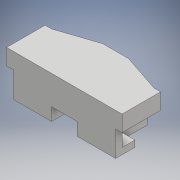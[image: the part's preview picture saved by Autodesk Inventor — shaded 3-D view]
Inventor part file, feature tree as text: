
AUTODESK INVENTOR PART (.ipt)
format: ipt  version: 2017 (Build 210142000, 142)  size: 303,104 bytes
history: native  units: mm
features: extrude x22, sketch x22, projected_geometry x2
ambient origin geometry x8: Origin, YZ Plane, XZ Plane, XY Plane, X Axis, Y Axis, Z Axis, Center Point
bodies: Solid1 (feature_tree)
feature tree (46):
  extrude  "Extrusion1"  Depth=60.0mm
  extrude  "Extrusion2"  Depth=10.0mm
  extrude  "Extrusion3"  Depth=160.0mm
  extrude  "Extrusion4"  Depth=70.0mm TaperAngle=0.0deg
  extrude  "Extrusion5"  Depth=10.0mm
  extrude  "Extrusion6"  Depth=10.0mm TaperAngle=0.0deg
  extrude  "Extrusion7"  Depth=50.0mm
  extrude  "Extrusion8"  Depth=50.0mm
  extrude  "Extrusion9"  Depth=10.0mm
  extrude  "Extrusion10"  Depth=10.0mm TaperAngle=0.0deg
  extrude  "Extrusion11"  Depth=60.0mm
  extrude  "Extrusion12"  Depth=60.0mm
  extrude  "Extrusion13"  Depth=10.0mm TaperAngle=0.0deg
  extrude  "Extrusion14"  Depth=10.0mm TaperAngle=0.0deg
  extrude  "Extrusion15"  Depth=160.0mm
  extrude  "Extrusion16"  Depth=20.0mm TaperAngle=0.0deg
  extrude  "Extrusion17"  Depth=15.0mm
  extrude  "Extrusion18"  Depth=15.0mm
  extrude  "Extrusion19"  Depth=10.0mm TaperAngle=0.0deg
  extrude  "Extrusion20"  Depth=10.0mm TaperAngle=0.0deg
  extrude  "Extrusion21"  Depth=60.0mm
  extrude  "Extrusion22"  Depth=20.0mm
  sketch  "Sketch1"  dims[d0=160.0mm d1=60.0mm]
  sketch  "Sketch2"  dims[d2=80.0mm d3=0.0mm d4=10.0mm]
  sketch  "Sketch3"  dims[d5=10.0mm d6=160.0mm]
  sketch  "Sketch4"  dims[d7=30.0mm d8=70.0mm d9=0.0mm]
  sketch  "Sketch5"  dims[d10=160.0mm d11=10.0mm]
  sketch  "Sketch6"  dims[d12=10.0mm d13=0.0mm d14=10.0mm d15=0.0mm]
  sketch  "Sketch7"  dims[d16=20.0mm d17=50.0mm]
  sketch  "Sketch8"  dims[d18=20.0mm d19=50.0mm]
  sketch  "Sketch9"  dims[d20=10.0mm d21=0.0mm d22=120.0mm]
  sketch  "Sketch11"  dims[d23=10.0mm d24=10.0mm d25=0.0mm]
  sketch  "Sketch12"  dims[d26=20.0mm d27=60.0mm]
  projected_geometry  "Projected Loop1"
  sketch  "Sketch13"  dims[d28=20.0mm d29=60.0mm]
  sketch  "Sketch14"  dims[d30=10.0mm d31=0.0mm d32=0.5mm d33=0.0mm]
  sketch  "Sketch15"  dims[d34=0.5mm d35=0.0mm d36=10.0mm d37=0.0mm]
  sketch  "Sketch16"  dims[d38=5.0mm d39=0.0mm d40=160.0mm]
  sketch  "Sketch17"  dims[d41=15.0mm d42=20.0mm d43=0.0mm]
  sketch  "Sketch18"  dims[d44=60.0mm d45=15.0mm]
  projected_geometry  "Projected Loop2"
  sketch  "Sketch19"  dims[d46=60.0mm d47=15.0mm]
  sketch  "Sketch20"  dims[d48=20.0mm d49=0.0mm d50=10.0mm d51=0.0mm]
  sketch  "Sketch21"  dims[d52=10.0mm d53=0.0mm d54=10.0mm d55=0.0mm]
  sketch  "Sketch22"  dims[d56=5.0mm d57=0.0mm d58=60.0mm]
  sketch  "Sketch23"  dims[d59=40.0mm d60=20.0mm d61=20.0mm d62=0.0mm d63=5.0mm d64=0.0mm d65=10.0mm d66=0.0mm d67=15.0mm d68=0.0mm d69=5.0mm d70=0.0mm]
